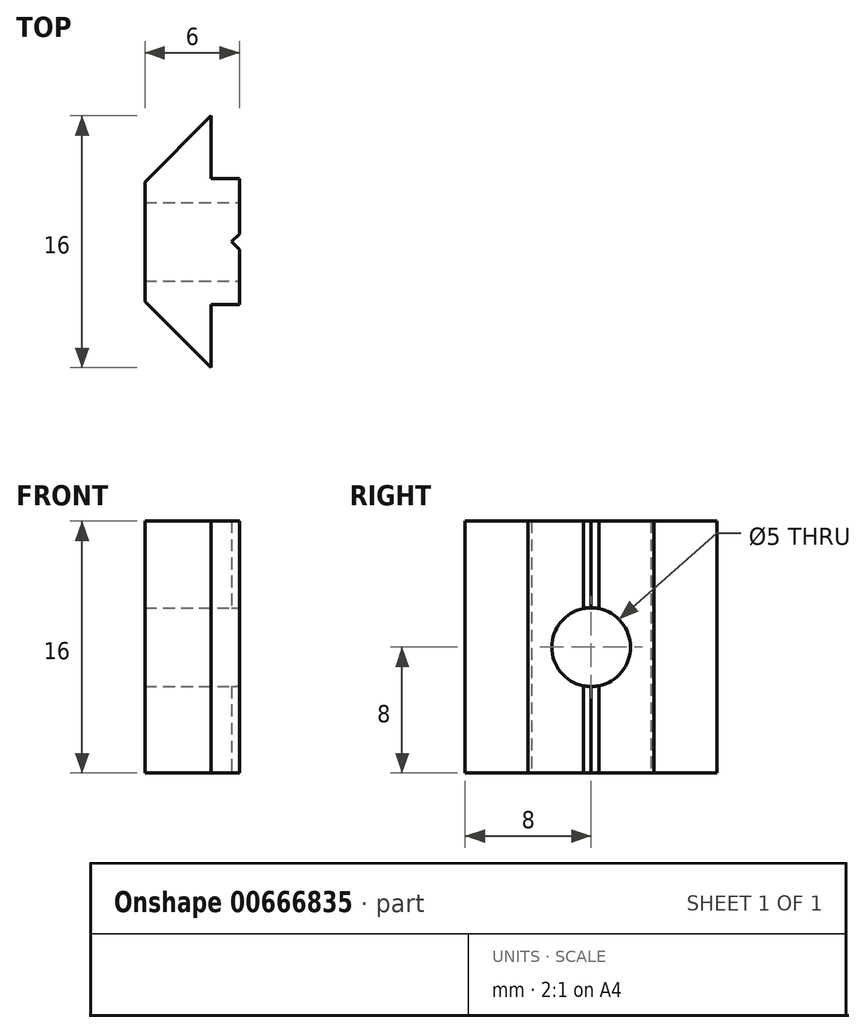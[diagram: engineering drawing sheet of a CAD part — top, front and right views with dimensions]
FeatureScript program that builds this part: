
annotation { "Feature Type Name" : "Feature", "Feature Type Description" : "" }
export const myFeature = defineFeature(function(context is Context, id is Id, definition is map)
    precondition{}
    {
        {
            var Q0;
            Q0=qCreatedBy(makeId("Top.planeOp"),FACE);
            var sketch = newSketch(context, id + "F0", { "sketchPlane" : qUnion([Q0])});
            skLineSegment(sketch, "E0", {"start": v(0, 0.5) * mm, "end": v(0, 4) * mm});
            skLineSegment(sketch, "E1", {"start": v(-6, 0) * mm, "end": v(-6, 3.8) * mm});
            skLineSegment(sketch, "E2", {"start": v(-6, 3.8) * mm, "end": v(-1.8, 8) * mm});
            skLineSegment(sketch, "E3", {"start": v(-1.8, 8) * mm, "end": v(-1.8, 4) * mm});
            skLineSegment(sketch, "E4", {"start": v(0, 4) * mm, "end": v(-1.8, 4) * mm});
            skLineSegment(sketch, "E5.MirrorCS", {"start": v(-6, -3.8) * mm, "end": v(-1.8, -8) * mm});
            skLineSegment(sketch, "E6.MirrorCS", {"start": v(-6, 0) * mm, "end": v(-6, -3.8) * mm});
            skLineSegment(sketch, "E7.MirrorCS", {"start": v(0, -0.5) * mm, "end": v(0, -4) * mm});
            skLineSegment(sketch, "E8.MirrorCS", {"start": v(-1.8, -8) * mm, "end": v(-1.8, -4) * mm});
            skLineSegment(sketch, "E9.MirrorCS", {"start": v(0, -4) * mm, "end": v(-1.8, -4) * mm});
            skLineSegment(sketch, "E10", {"start": v(0, 0.5) * mm, "end": v(-0.5, 0) * mm});
            skLineSegment(sketch, "E11", {"start": v(-0.5, 0) * mm, "end": v(0, -0.5) * mm});
            skPoint(sketch, "E12.orphan", {"position": v(0, 0) * mm});
            skSolve(sketch);
        }
        {
            var Q0;
            Q0=qSketchRegion(id+"F0",true);
            extrude(context, id + "F1", {"entities" : qUnion([Q0]), "depth" : 16 * mm, "offsetDistance" : 25 * mm});
        }
        {
            var Q0;
            Q0=makeQuery(id+"F1.opExtrude","SWEPT_FACE",FACE,{"disambiguationData":[OSD([sQuery(id+"F0.wireOp",EDGE,"E1"),sQuery(id+"F0.wireOp",EDGE,"E6.MirrorCS")])]});
            var sketch = newSketch(context, id + "F2", { "sketchPlane" : qUnion([Q0])});
            skLineSegment(sketch, "E13", {"start": v(0, 16) * mm, "end": v(0, 0) * mm, "construction": true});
            skPoint(sketch, "E14", {"position": v(0, 8) * mm});
            skSolve(sketch);
        }
        {
            var Q0;
            Q0=sQuery(id+"F2.wireOp",VERTEX,"E14");
            var Q1;
            Q1=makeQuery(id+"F1.opExtrude","SWEPT_BODY",BODY,{"disambiguationData":[OSD([sQuery(id+"F0.wireOp",EDGE,"E0"),sQuery(id+"F0.wireOp",EDGE,"E1"),sQuery(id+"F0.wireOp",EDGE,"E2"),sQuery(id+"F0.wireOp",EDGE,"E3"),sQuery(id+"F0.wireOp",EDGE,"E4"),sQuery(id+"F0.wireOp",EDGE,"E5.MirrorCS"),sQuery(id+"F0.wireOp",EDGE,"E6.MirrorCS"),sQuery(id+"F0.wireOp",EDGE,"E7.MirrorCS"),sQuery(id+"F0.wireOp",EDGE,"E8.MirrorCS"),sQuery(id+"F0.wireOp",EDGE,"E9.MirrorCS"),sQuery(id+"F0.wireOp",EDGE,"E10"),sQuery(id+"F0.wireOp",EDGE,"E11")])]});
            hole(context, id + "F3", {"style" : HoleStyle.SIMPLE, "endStyle" : HoleEndStyle.BLIND, "standardTappedOrClearance" : lookupTablePath({ "standard" : "ISO", "engagement" : "75%", "pitch" : "1 mm", "size" : "M6", "type" : "Tapped" }), "standardBlindInLast" : lookupTablePath({ "standard" : "ISO", "fit" : "Normal", "engagement" : "75%", "pitch" : "1 mm", "size" : "M6", "type" : "Clearance & tapped" }), "holeDiameter" : 5 * mm, "majorDiameter" : 6 * mm, "showTappedDepth" : true, "holeDepth" : 15 * mm, "isTappedThrough" : true, "tappedDepth" : 12 * mm, "tapClearance" : 3, "locations" : qUnion([Q0]), "scope" : qUnion([Q1])});
        }
    });
